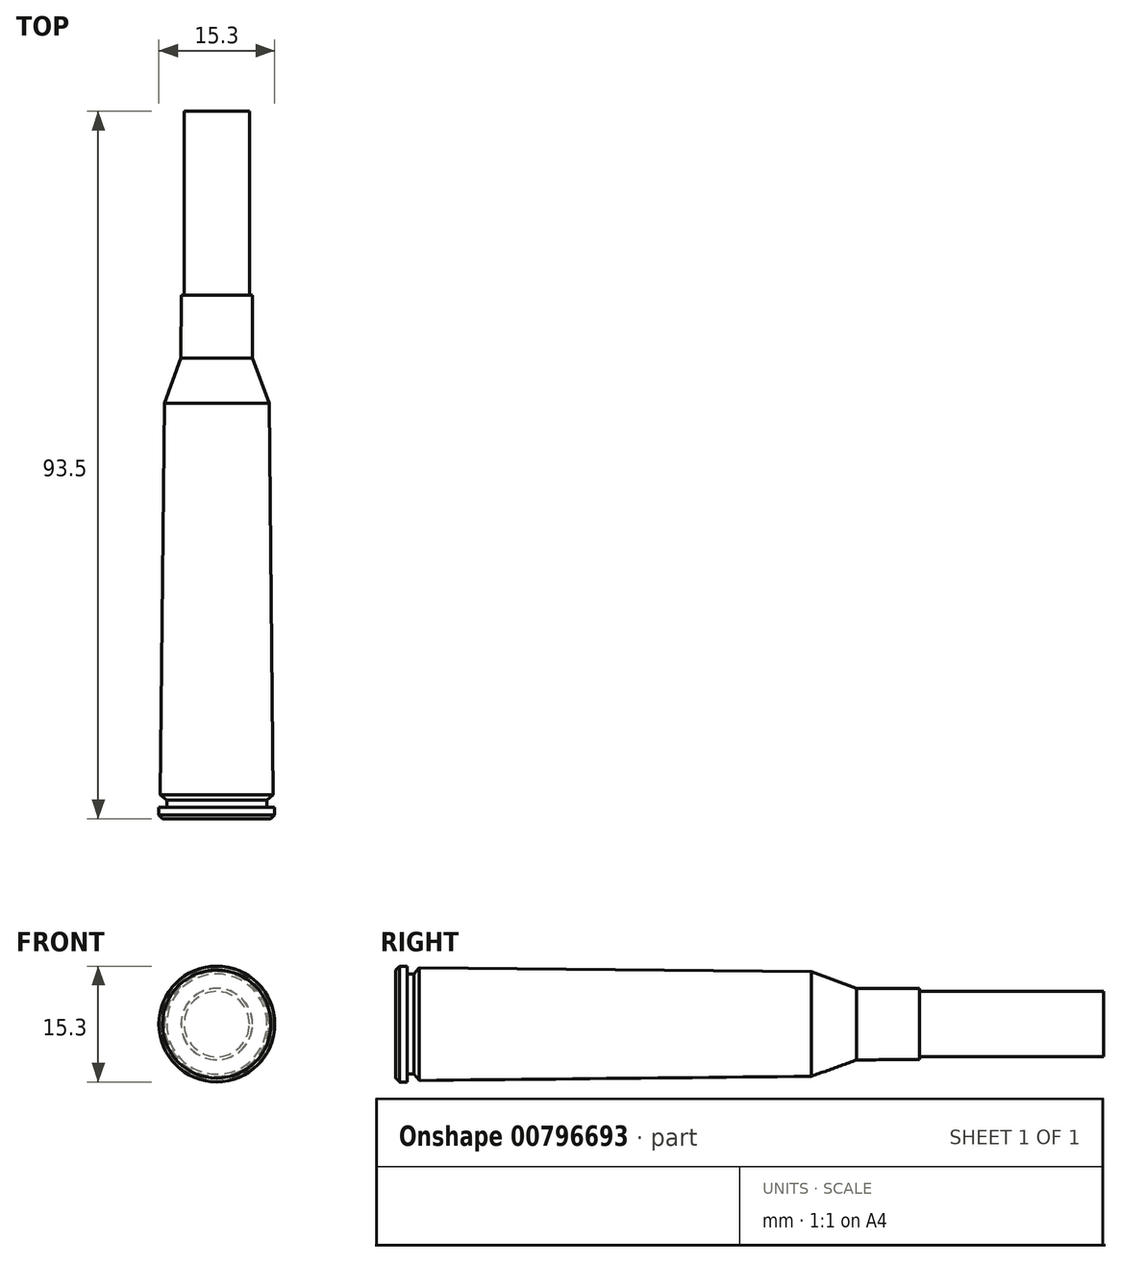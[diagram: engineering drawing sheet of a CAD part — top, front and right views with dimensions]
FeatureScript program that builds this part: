
annotation { "Feature Type Name" : "Feature", "Feature Type Description" : "" }
export const myFeature = defineFeature(function(context is Context, id is Id, definition is map)
    precondition{}
    {
        {
            var Q0;
            Q0=qCreatedBy(makeId("Right.planeOp"),FACE);
            var sketch = newSketch(context, id + "F0", { "sketchPlane" : qUnion([Q0])});
            skLineSegment(sketch, "E0", {"start": v(0, 0) * mm, "end": v(0.5, 0) * mm});
            skLineSegment(sketch, "E1", {"start": v(0, -3.15) * mm, "end": v(1.52, -3.15) * mm});
            skLineSegment(sketch, "E2", {"start": v(0, -4.82) * mm, "end": v(3.12, -4.82) * mm});
            skLineSegment(sketch, "E3", {"start": v(0, -6.6) * mm, "end": v(54.9, -6.6) * mm});
            skLineSegment(sketch, "E4", {"start": v(0, -10.15) * mm, "end": v(60.9, -10.15) * mm});
            skLineSegment(sketch, "E5", {"start": v(0, -15.94) * mm, "end": v(69.2, -15.94) * mm});
            skLineSegment(sketch, "E6", {"start": v(0, -22.75) * mm, "end": v(93.5, -22.75) * mm});
            skLineSegment(sketch, "E7", {"start": v(0.5, 0) * mm, "end": v(1.52, 0) * mm});
            skLineSegment(sketch, "E8", {"start": v(1.52, 0) * mm, "end": v(2.42, 0) * mm});
            skLineSegment(sketch, "E9", {"start": v(2.42, 0) * mm, "end": v(3.12, 0) * mm});
            skLineSegment(sketch, "E10", {"start": v(3.12, 0) * mm, "end": v(54.9, 0) * mm});
            skLineSegment(sketch, "E11", {"start": v(54.9, 0) * mm, "end": v(60.9, 0) * mm});
            skLineSegment(sketch, "E12", {"start": v(60.9, 0) * mm, "end": v(69.2, 0) * mm});
            skLineSegment(sketch, "E13", {"start": v(69.2, 0) * mm, "end": v(93.5, 0) * mm});
            skLineSegment(sketch, "E14", {"start": v(93.5, 0) * mm, "end": v(93.5, 4.3) * mm});
            skLineSegment(sketch, "E15", {"start": v(93.5, 4.3) * mm, "end": v(69.2, 4.3) * mm});
            skLineSegment(sketch, "E16", {"start": v(69.2, 0) * mm, "end": v(69.2, 4.7) * mm});
            skLineSegment(sketch, "E17", {"start": v(69.2, 4.7) * mm, "end": v(60.9, 4.73) * mm});
            skLineSegment(sketch, "E18", {"start": v(60.9, 4.73) * mm, "end": v(54.9, 6.91) * mm});
            skLineSegment(sketch, "E19", {"start": v(54.9, 6.9) * mm, "end": v(54.9, 0) * mm});
            skLineSegment(sketch, "E20", {"start": v(60.9, 0) * mm, "end": v(60.9, 4.73) * mm});
            skLineSegment(sketch, "E21", {"start": v(54.9, 6.9) * mm, "end": v(3.12, 7.46) * mm});
            skLineSegment(sketch, "E22", {"start": v(3.12, 7.46) * mm, "end": v(3.12, 0) * mm});
            skLineSegment(sketch, "E23", {"start": v(2.42, 0) * mm, "end": v(2.42, 6.62) * mm});
            skLineSegment(sketch, "E24", {"start": v(2.42, 6.62) * mm, "end": v(3.12, 7.45) * mm});
            skLineSegment(sketch, "E25", {"start": v(2.42, 6.62) * mm, "end": v(1.52, 6.62) * mm});
            skLineSegment(sketch, "E26", {"start": v(1.52, 0) * mm, "end": v(1.52, 7.65) * mm});
            skLineSegment(sketch, "E27", {"start": v(1.52, 7.65) * mm, "end": v(0.5, 7.65) * mm});
            skLineSegment(sketch, "E28", {"start": v(0.5, 7.65) * mm, "end": v(0, 7.15) * mm});
            skLineSegment(sketch, "E29", {"start": v(0, 7.15) * mm, "end": v(0, 0) * mm});
            skSolve(sketch);
        }
        {
            var Q0;
            Q0=makeQuery(id+"F0.imprint","IMPRINT",FACE,{"disambiguationData":[TD([[makeQuery(id+"F0.imprint","IMPRINT",EDGE,{"derivedFrom":sQuery(id+"F0.wireOp",EDGE,"E0")}),1.0]])]});
            var Q1;
            {var subQ0=sQuery(id+"F0.wireOp",EDGE,"E8");Q1=makeQuery(id+"F0.imprint","IMPRINT",FACE,{"disambiguationData":[TD([[makeQuery(id+"F0.imprint","IMPRINT",EDGE,{"derivedFrom":subQ0}),1.0]])]});}
            var Q2;
            Q2=makeQuery(id+"F0.imprint","IMPRINT",FACE,{"disambiguationData":[TD([[makeQuery(id+"F0.imprint","IMPRINT",EDGE,{"derivedFrom":sQuery(id+"F0.wireOp",EDGE,"E9")}),1.0]])]});
            var Q3;
            Q3=makeQuery(id+"F0.imprint","IMPRINT",FACE,{"disambiguationData":[TD([[makeQuery(id+"F0.imprint","IMPRINT",EDGE,{"derivedFrom":sQuery(id+"F0.wireOp",EDGE,"E10")}),1.0]])]});
            var Q4;
            Q4=makeQuery(id+"F0.imprint","IMPRINT",FACE,{"disambiguationData":[TD([[makeQuery(id+"F0.imprint","IMPRINT",EDGE,{"derivedFrom":sQuery(id+"F0.wireOp",EDGE,"E11")}),1.0]])]});
            var Q5;
            {var subQ2=sQuery(id+"F0.wireOp",EDGE,"E12");Q5=makeQuery(id+"F0.imprint","IMPRINT",FACE,{"disambiguationData":[TD([[makeQuery(id+"F0.imprint","IMPRINT",EDGE,{"derivedFrom":subQ2}),1.0]])]});}
            var Q6;
            {var subQ0=sQuery(id+"F0.wireOp",EDGE,"E13");Q6=makeQuery(id+"F0.imprint","IMPRINT",FACE,{"disambiguationData":[TD([[makeQuery(id+"F0.imprint","IMPRINT",EDGE,{"derivedFrom":subQ0}),1.0]])]});}
            var Q7;
            Q7=sQuery(id+"F0.wireOp",EDGE,"E10");
            revolve(context, id + "F1", {"surfaceOperationType" : NewSurfaceOperationType.NEW, "entities" : qUnion([Q0, Q1, Q2, Q3, Q4, Q5, Q6]), "axis" : qUnion([Q7]), "revolveType" : RevolveType.FULL});
        }
    });
